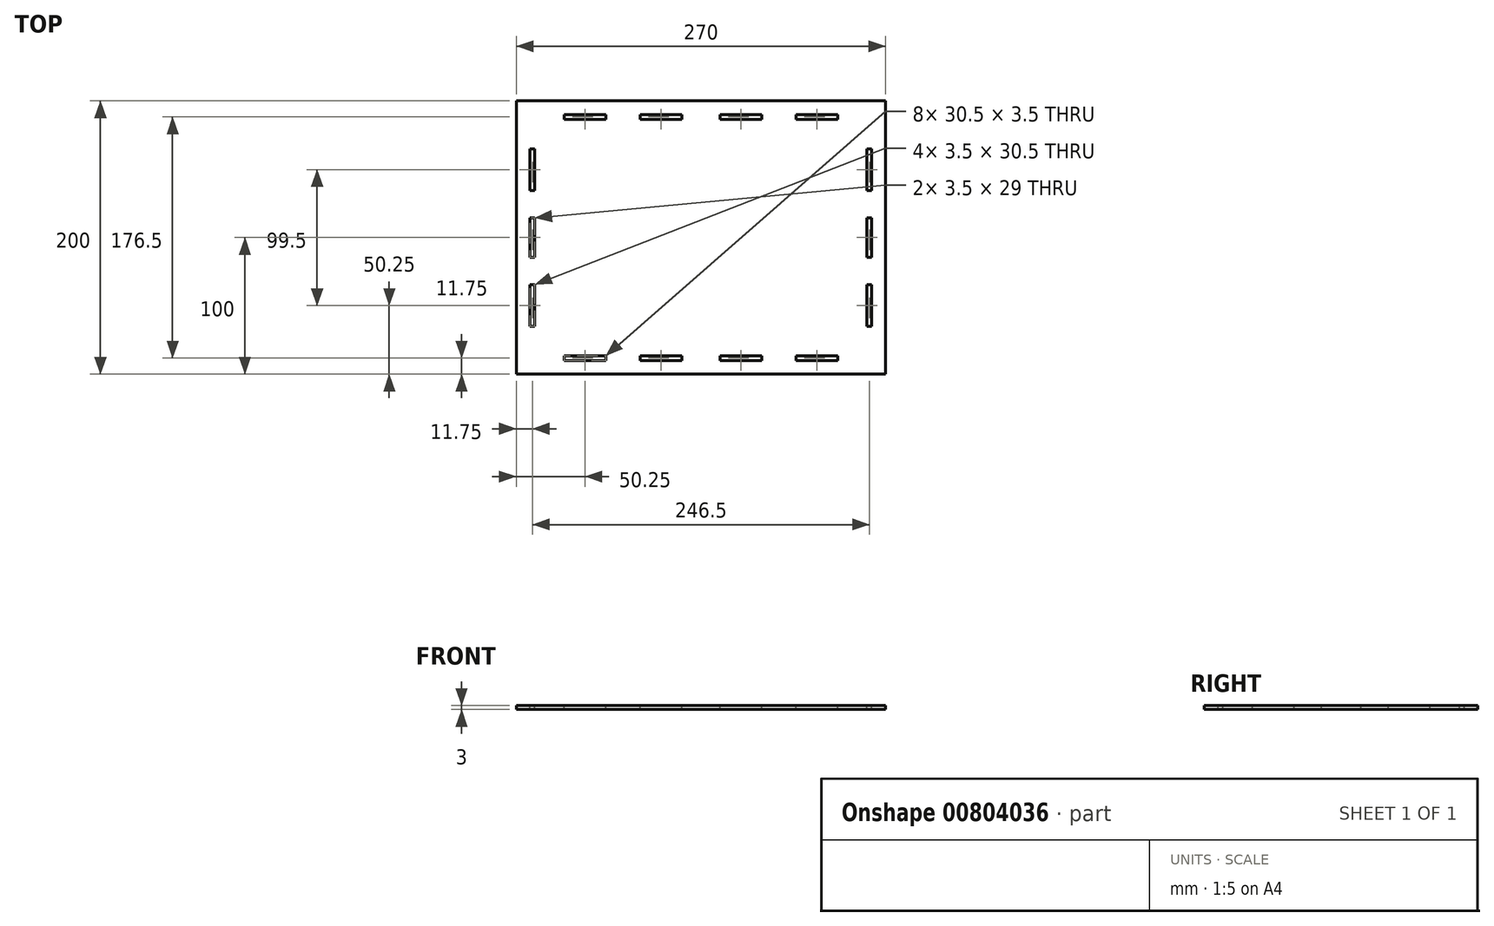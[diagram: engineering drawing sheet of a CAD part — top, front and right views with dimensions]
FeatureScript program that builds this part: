
annotation { "Feature Type Name" : "Feature", "Feature Type Description" : "" }
export const myFeature = defineFeature(function(context is Context, id is Id, definition is map)
    precondition{}
    {
        {
            var Q0;
            Q0=qCreatedBy(makeId("Top.planeOp"),FACE);
            var sketch = newSketch(context, id + "F0", { "sketchPlane" : qUnion([Q0])});
            skLineSegment(sketch, "E0.bottom", {"start": v(-135, 100) * mm, "end": v(135, 100) * mm});
            skLineSegment(sketch, "E0.top", {"start": v(-135, -100) * mm, "end": v(135, -100) * mm});
            skLineSegment(sketch, "E0.left", {"start": v(-135, 100) * mm, "end": v(-135, -100) * mm});
            skLineSegment(sketch, "E0.right", {"start": v(135, 100) * mm, "end": v(135, -100) * mm});
            skPoint(sketch, "E0.middle", {"position": v(0, 0) * mm});
            skSolve(sketch);
        }
        {
            var Q0;
            Q0=makeQuery(id+"F0.imprint","IMPRINT",FACE,{"disambiguationData":[TD([[makeQuery(id+"F0.imprint","IMPRINT",EDGE,{"derivedFrom":sQuery(id+"F0.wireOp",EDGE,"E0.bottom")}),-1.0]])]});
            extrude(context, id + "F1", {"entities" : qUnion([Q0]), "depth" : 3 * mm, "offsetDistance" : 25 * mm});
        }
        {
            var Q0;
            Q0=makeQuery(id+"F1.opExtrude","CAP_FACE",FACE,{"disambiguationData":[OSD([sQuery(id+"F0.wireOp",EDGE,"E0.bottom"),sQuery(id+"F0.wireOp",EDGE,"E0.top"),sQuery(id+"F0.wireOp",EDGE,"E0.left"),sQuery(id+"F0.wireOp",EDGE,"E0.right")])],"isStart":false});
            var sketch = newSketch(context, id + "F2", { "sketchPlane" : qUnion([Q0])});
            skPoint(sketch, "E1.middle", {"position": v(0, 0) * mm});
            skLineSegment(sketch, "E2", {"start": v(100, 90) * mm, "end": v(100, 86.5) * mm});
            skLineSegment(sketch, "E3", {"start": v(100, 86.5) * mm, "end": v(69.5, 86.5) * mm});
            skLineSegment(sketch, "E4", {"start": v(69.5, 86.5) * mm, "end": v(69.5, 90) * mm});
            skLineSegment(sketch, "E5", {"start": v(69.5, 90) * mm, "end": v(100, 90) * mm});
            skLineSegment(sketch, "E6", {"start": v(44.5, 90) * mm, "end": v(44.5, 86.5) * mm});
            skLineSegment(sketch, "E7", {"start": v(44.5, 86.5) * mm, "end": v(14, 86.5) * mm});
            skLineSegment(sketch, "E8", {"start": v(14, 86.5) * mm, "end": v(14, 90) * mm});
            skLineSegment(sketch, "E9", {"start": v(14, 90) * mm, "end": v(44.5, 90) * mm});
            skLineSegment(sketch, "E10", {"start": v(125, 65) * mm, "end": v(121.5, 65) * mm});
            skLineSegment(sketch, "E11", {"start": v(121.5, 65) * mm, "end": v(121.5, 34.5) * mm});
            skLineSegment(sketch, "E12", {"start": v(121.5, 34.5) * mm, "end": v(125, 34.5) * mm});
            skLineSegment(sketch, "E13", {"start": v(125, 34.5) * mm, "end": v(125, 65) * mm});
            skLineSegment(sketch, "E14.MirrorCS", {"start": v(-100, 90) * mm, "end": v(-100, 86.5) * mm});
            skLineSegment(sketch, "E15.MirrorCS", {"start": v(-14, 86.5) * mm, "end": v(-14, 90) * mm});
            skLineSegment(sketch, "E16.MirrorCS", {"start": v(-69.5, 86.5) * mm, "end": v(-69.5, 90) * mm});
            skLineSegment(sketch, "E17.MirrorCS", {"start": v(-44.5, 90) * mm, "end": v(-44.5, 86.5) * mm});
            skLineSegment(sketch, "E18.MirrorCS", {"start": v(-14, 90) * mm, "end": v(-44.5, 90) * mm});
            skLineSegment(sketch, "E19.MirrorCS", {"start": v(-100, 86.5) * mm, "end": v(-69.5, 86.5) * mm});
            skLineSegment(sketch, "E20.MirrorCS", {"start": v(-69.5, 90) * mm, "end": v(-100, 90) * mm});
            skLineSegment(sketch, "E21.MirrorCS", {"start": v(-44.5, 86.5) * mm, "end": v(-14, 86.5) * mm});
            skLineSegment(sketch, "E22.MirrorCS", {"start": v(-100, -90) * mm, "end": v(-100, -86.5) * mm});
            skLineSegment(sketch, "E23.MirrorCS", {"start": v(-69.5, -86.5) * mm, "end": v(-69.5, -90) * mm});
            skLineSegment(sketch, "E24.MirrorCS", {"start": v(44.5, -90) * mm, "end": v(44.5, -86.5) * mm});
            skLineSegment(sketch, "E25.MirrorCS", {"start": v(14, -86.5) * mm, "end": v(14, -90) * mm});
            skLineSegment(sketch, "E26.MirrorCS", {"start": v(-44.5, -90) * mm, "end": v(-44.5, -86.5) * mm});
            skLineSegment(sketch, "E27.MirrorCS", {"start": v(-14, -86.5) * mm, "end": v(-14, -90) * mm});
            skLineSegment(sketch, "E28.MirrorCS", {"start": v(69.5, -86.5) * mm, "end": v(69.5, -90) * mm});
            skLineSegment(sketch, "E29.MirrorCS", {"start": v(100, -90) * mm, "end": v(100, -86.5) * mm});
            skLineSegment(sketch, "E30.MirrorCS", {"start": v(100, -86.5) * mm, "end": v(69.5, -86.5) * mm});
            skLineSegment(sketch, "E31.MirrorCS", {"start": v(44.5, -86.5) * mm, "end": v(14, -86.5) * mm});
            skLineSegment(sketch, "E32.MirrorCS", {"start": v(14, -90) * mm, "end": v(44.5, -90) * mm});
            skLineSegment(sketch, "E33.MirrorCS", {"start": v(-14, -90) * mm, "end": v(-44.5, -90) * mm});
            skLineSegment(sketch, "E34.MirrorCS", {"start": v(-100, -86.5) * mm, "end": v(-69.5, -86.5) * mm});
            skLineSegment(sketch, "E35.MirrorCS", {"start": v(-44.5, -86.5) * mm, "end": v(-14, -86.5) * mm});
            skLineSegment(sketch, "E36.MirrorCS", {"start": v(-69.5, -90) * mm, "end": v(-100, -90) * mm});
            skLineSegment(sketch, "E37.MirrorCS", {"start": v(69.5, -90) * mm, "end": v(100, -90) * mm});
            skLineSegment(sketch, "E38.MirrorCS", {"start": v(121.5, -34.5) * mm, "end": v(125, -34.5) * mm});
            skLineSegment(sketch, "E39.MirrorCS", {"start": v(121.5, -65) * mm, "end": v(121.5, -34.5) * mm});
            skLineSegment(sketch, "E40.MirrorCS", {"start": v(125, -34.5) * mm, "end": v(125, -65) * mm});
            skLineSegment(sketch, "E41.MirrorCS", {"start": v(125, -65) * mm, "end": v(121.5, -65) * mm});
            skLineSegment(sketch, "E42.MirrorCS", {"start": v(-125, -65) * mm, "end": v(-121.5, -65) * mm});
            skLineSegment(sketch, "E43.MirrorCS", {"start": v(-121.5, -34.5) * mm, "end": v(-125, -34.5) * mm});
            skLineSegment(sketch, "E44.MirrorCS", {"start": v(-125, 65) * mm, "end": v(-121.5, 65) * mm});
            skLineSegment(sketch, "E45.MirrorCS", {"start": v(-121.5, 34.5) * mm, "end": v(-125, 34.5) * mm});
            skLineSegment(sketch, "E46.MirrorCS", {"start": v(-121.5, 65) * mm, "end": v(-121.5, 34.5) * mm});
            skLineSegment(sketch, "E47.MirrorCS", {"start": v(-125, 34.5) * mm, "end": v(-125, 65) * mm});
            skLineSegment(sketch, "E48.MirrorCS", {"start": v(-125, -34.5) * mm, "end": v(-125, -65) * mm});
            skLineSegment(sketch, "E49.MirrorCS", {"start": v(-121.5, -65) * mm, "end": v(-121.5, -34.5) * mm});
            skLineSegment(sketch, "E50", {"start": v(125, -14.5) * mm, "end": v(121.5, -14.5) * mm});
            skLineSegment(sketch, "E51", {"start": v(121.5, -14.5) * mm, "end": v(121.5, 14.5) * mm});
            skLineSegment(sketch, "E52", {"start": v(121.5, 14.5) * mm, "end": v(125, 14.5) * mm});
            skLineSegment(sketch, "E53", {"start": v(125, 14.5) * mm, "end": v(125, -14.5) * mm});
            skLineSegment(sketch, "E54.MirrorCS", {"start": v(-121.5, 14.5) * mm, "end": v(-125, 14.5) * mm});
            skLineSegment(sketch, "E55.MirrorCS", {"start": v(-121.5, -14.5) * mm, "end": v(-121.5, 14.5) * mm});
            skLineSegment(sketch, "E56.MirrorCS", {"start": v(-125, 14.5) * mm, "end": v(-125, -14.5) * mm});
            skLineSegment(sketch, "E57.MirrorCS", {"start": v(-125, -14.5) * mm, "end": v(-121.5, -14.5) * mm});
            skLineSegment(sketch, "E58", {"start": v(-100, -90) * mm, "end": v(-125, -90) * mm});
            skLineSegment(sketch, "E59", {"start": v(-100, -86.5) * mm, "end": v(-69.5, -90) * mm});
            skLineSegment(sketch, "E60", {"start": v(-69.5, -86.5) * mm, "end": v(-100, -90) * mm});
            skLineSegment(sketch, "E61", {"start": v(-84.75, -88.25) * mm, "end": v(-84.75, -100) * mm});
            skLineSegment(sketch, "E62", {"start": v(-44.5, -86.5) * mm, "end": v(-14, -90) * mm});
            skLineSegment(sketch, "E63", {"start": v(-44.5, -90) * mm, "end": v(-14, -86.5) * mm});
            skLineSegment(sketch, "E64", {"start": v(-29.25, -88.25) * mm, "end": v(-29.25, -100) * mm});
            skSolve(sketch);
        }
        {
            var Q0;
            Q0 = qSketchRegion(id + "F2", true);
            extrude(context, id + "F3", {"entities" : qUnion([Q0]), "operationType" : NewBodyOperationType.REMOVE, "oppositeDirection" : true, "depth" : 3 * mm, "offsetDistance" : 25 * mm});
        }
    });
